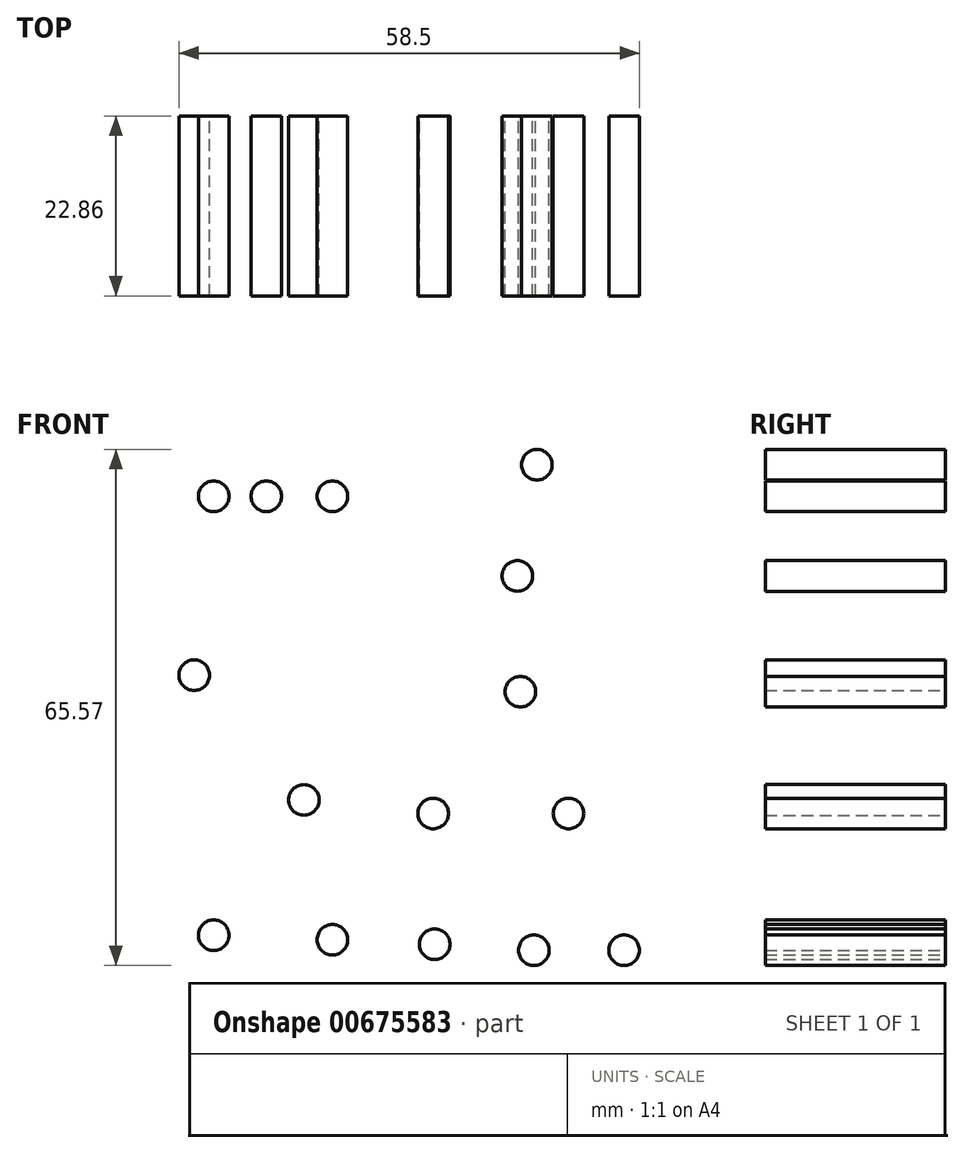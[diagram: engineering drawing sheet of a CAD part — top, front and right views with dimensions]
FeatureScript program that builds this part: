
annotation { "Feature Type Name" : "Feature", "Feature Type Description" : "" }
export const myFeature = defineFeature(function(context is Context, id is Id, definition is map)
    precondition{}
    {
        {
            var Q0;
            Q0=qCreatedBy(makeId("Front.planeOp"),FACE);
            var sketch = newSketch(context, id + "F0", { "sketchPlane" : qUnion([Q0])});
            skCircle(sketch, "E0", {"center": v(-60.25, 43.44) * mm, "radius": 1.95 * mm});
            skCircle(sketch, "E1", {"center": v(-53.56, 43.44) * mm, "radius": 1.94 * mm});
            skCircle(sketch, "E2", {"center": v(-45.16, 43.44) * mm, "radius": 1.94 * mm});
            skCircle(sketch, "E3", {"center": v(-62.73, 20.72) * mm, "radius": 1.94 * mm});
            skCircle(sketch, "E4", {"center": v(-21.3, 18.62) * mm, "radius": 1.94 * mm});
            skPoint(sketch, "E5.center.orphan", {"position": v(-39.62, 20.34) * mm});
            skPoint(sketch, "E6.center.orphan", {"position": v(-50.13, 20.34) * mm});
            skCircle(sketch, "E7", {"center": v(-21.67, 33.32) * mm, "radius": 1.94 * mm});
            skCircle(sketch, "E8", {"center": v(-19.2, 47.45) * mm, "radius": 1.94 * mm});
            skCircle(sketch, "E9", {"center": v(-48.79, 4.87) * mm, "radius": 1.94 * mm});
            skCircle(sketch, "E10", {"center": v(-32.37, 3.15) * mm, "radius": 1.94 * mm});
            skCircle(sketch, "E11", {"center": v(-15.18, 3.15) * mm, "radius": 1.94 * mm});
            skCircle(sketch, "E12", {"center": v(-60.25, -12.32) * mm, "radius": 1.94 * mm});
            skCircle(sketch, "E13", {"center": v(-45.16, -12.89) * mm, "radius": 1.94 * mm});
            skCircle(sketch, "E14", {"center": v(-32.18, -13.46) * mm, "radius": 1.94 * mm});
            skCircle(sketch, "E15", {"center": v(-19.57, -14.23) * mm, "radius": 1.94 * mm});
            skCircle(sketch, "E16", {"center": v(-8.12, -14.23) * mm, "radius": 1.94 * mm});
            skSolve(sketch);
        }
        {
            var Q0;
            Q0 = qSketchRegion(id + "F0", true);
            extrude(context, id + "F1", {"entities" : qUnion([Q0]), "depth" : 22.86 * mm, "offsetDistance" : 25.4 * mm});
        }
    });
